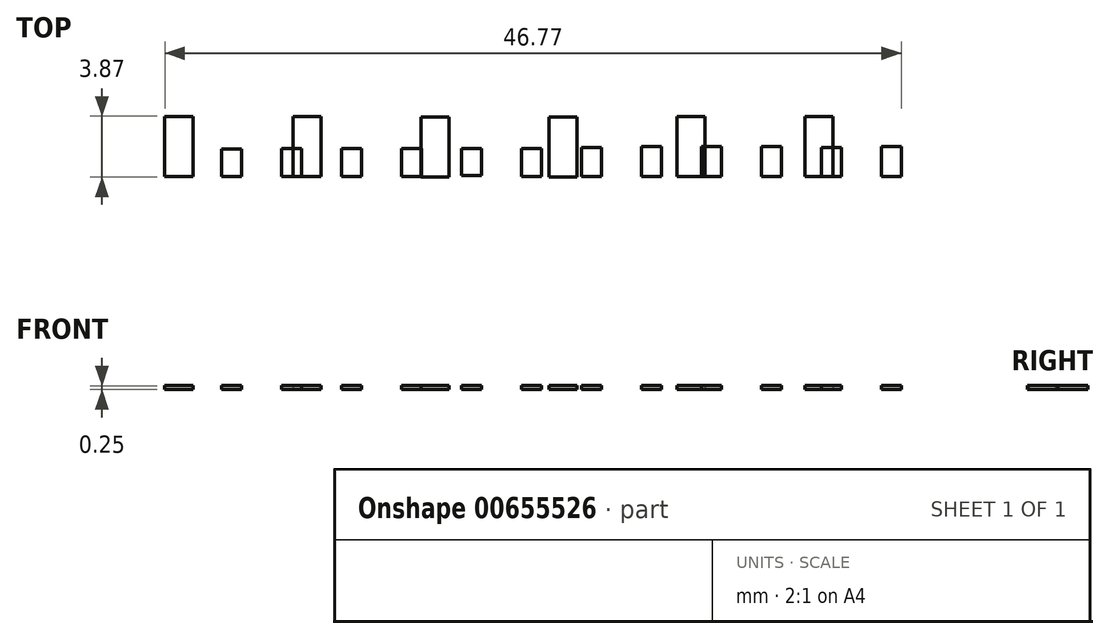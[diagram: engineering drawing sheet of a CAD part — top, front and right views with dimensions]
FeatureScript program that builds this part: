
annotation { "Feature Type Name" : "Feature", "Feature Type Description" : "" }
export const myFeature = defineFeature(function(context is Context, id is Id, definition is map)
    precondition{}
    {
        {
            var Q0;
            Q0=qCreatedBy(makeId("Top.planeOp"),FACE);
            var sketch = newSketch(context, id + "F0", { "sketchPlane" : qUnion([Q0])});
            skLineSegment(sketch, "E0.bottom", {"start": v(2.28, -12.7) * mm, "end": v(1.01, -12.7) * mm});
            skLineSegment(sketch, "E0.top", {"start": v(2.28, -10.86) * mm, "end": v(1.01, -10.86) * mm});
            skLineSegment(sketch, "E0.left", {"start": v(2.28, -12.7) * mm, "end": v(2.28, -10.86) * mm});
            skLineSegment(sketch, "E0.right", {"start": v(1.01, -12.7) * mm, "end": v(1.01, -10.86) * mm});
            skLineSegment(sketch, "E1.bottom", {"start": v(-1.53, -12.69) * mm, "end": v(-2.8, -12.69) * mm});
            skLineSegment(sketch, "E1.top", {"start": v(-1.53, -10.91) * mm, "end": v(-2.8, -10.91) * mm});
            skLineSegment(sketch, "E1.left", {"start": v(-1.53, -12.69) * mm, "end": v(-1.53, -10.91) * mm});
            skLineSegment(sketch, "E1.right", {"start": v(-2.8, -12.69) * mm, "end": v(-2.8, -10.91) * mm});
            skLineSegment(sketch, "E2.bottom", {"start": v(-5.34, -12.64) * mm, "end": v(-6.6, -12.64) * mm});
            skLineSegment(sketch, "E2.top", {"start": v(-5.34, -10.92) * mm, "end": v(-6.6, -10.92) * mm});
            skLineSegment(sketch, "E2.left", {"start": v(-5.34, -12.64) * mm, "end": v(-5.34, -10.92) * mm});
            skLineSegment(sketch, "E2.right", {"start": v(-6.6, -12.64) * mm, "end": v(-6.6, -10.92) * mm});
            skLineSegment(sketch, "E3.bottom", {"start": v(-9.15, -12.71) * mm, "end": v(-10.42, -12.71) * mm});
            skLineSegment(sketch, "E3.top", {"start": v(-9.15, -10.93) * mm, "end": v(-10.42, -10.93) * mm});
            skLineSegment(sketch, "E3.left", {"start": v(-9.15, -12.71) * mm, "end": v(-9.15, -10.93) * mm});
            skLineSegment(sketch, "E3.right", {"start": v(-10.42, -12.71) * mm, "end": v(-10.42, -10.93) * mm});
            skLineSegment(sketch, "E4.bottom", {"start": v(-12.96, -12.71) * mm, "end": v(-14.23, -12.71) * mm});
            skLineSegment(sketch, "E4.top", {"start": v(-12.96, -10.93) * mm, "end": v(-14.23, -10.93) * mm});
            skLineSegment(sketch, "E4.left", {"start": v(-12.96, -12.71) * mm, "end": v(-12.96, -10.93) * mm});
            skLineSegment(sketch, "E4.right", {"start": v(-14.23, -12.71) * mm, "end": v(-14.23, -10.93) * mm});
            skPoint(sketch, "E5.oppositeSnap0", {"position": v(-13.6, -10.93) * mm});
            skLineSegment(sketch, "E5.bottom", {"start": v(-16.77, -12.71) * mm, "end": v(-18.04, -12.71) * mm});
            skLineSegment(sketch, "E5.top", {"start": v(-16.77, -10.93) * mm, "end": v(-18.04, -10.93) * mm});
            skLineSegment(sketch, "E5.left", {"start": v(-16.77, -12.71) * mm, "end": v(-16.77, -10.93) * mm});
            skLineSegment(sketch, "E5.right", {"start": v(-18.04, -12.71) * mm, "end": v(-18.04, -10.93) * mm});
            skLineSegment(sketch, "E6.bottom", {"start": v(-20.58, -12.7) * mm, "end": v(-21.85, -12.7) * mm});
            skLineSegment(sketch, "E6.top", {"start": v(-20.58, -10.95) * mm, "end": v(-21.85, -10.95) * mm});
            skLineSegment(sketch, "E6.left", {"start": v(-20.58, -12.7) * mm, "end": v(-20.58, -10.95) * mm});
            skLineSegment(sketch, "E6.right", {"start": v(-21.85, -12.7) * mm, "end": v(-21.85, -10.95) * mm});
            skLineSegment(sketch, "E7.bottom", {"start": v(6.1, -12.7) * mm, "end": v(4.82, -12.7) * mm});
            skLineSegment(sketch, "E7.top", {"start": v(6.1, -10.8) * mm, "end": v(4.82, -10.8) * mm});
            skLineSegment(sketch, "E7.left", {"start": v(6.1, -12.7) * mm, "end": v(6.1, -10.8) * mm});
            skLineSegment(sketch, "E7.right", {"start": v(4.82, -12.7) * mm, "end": v(4.82, -10.8) * mm});
            skLineSegment(sketch, "E8.bottom", {"start": v(9.9, -12.7) * mm, "end": v(8.63, -12.7) * mm});
            skLineSegment(sketch, "E8.top", {"start": v(9.9, -10.8) * mm, "end": v(8.63, -10.8) * mm});
            skLineSegment(sketch, "E8.left", {"start": v(9.9, -12.7) * mm, "end": v(9.9, -10.8) * mm});
            skLineSegment(sketch, "E8.right", {"start": v(8.63, -12.7) * mm, "end": v(8.63, -10.8) * mm});
            skLineSegment(sketch, "E9.bottom", {"start": v(13.71, -12.7) * mm, "end": v(12.44, -12.7) * mm});
            skLineSegment(sketch, "E9.top", {"start": v(13.71, -10.8) * mm, "end": v(12.44, -10.8) * mm});
            skLineSegment(sketch, "E9.left", {"start": v(13.71, -12.7) * mm, "end": v(13.71, -10.8) * mm});
            skLineSegment(sketch, "E9.right", {"start": v(12.44, -12.7) * mm, "end": v(12.44, -10.8) * mm});
            skLineSegment(sketch, "E10.bottom", {"start": v(17.52, -12.7) * mm, "end": v(16.25, -12.7) * mm});
            skLineSegment(sketch, "E10.top", {"start": v(17.52, -10.85) * mm, "end": v(16.25, -10.85) * mm});
            skLineSegment(sketch, "E10.left", {"start": v(17.52, -12.7) * mm, "end": v(17.52, -10.85) * mm});
            skLineSegment(sketch, "E10.right", {"start": v(16.25, -12.7) * mm, "end": v(16.25, -10.85) * mm});
            skLineSegment(sketch, "E11.bottom", {"start": v(21.33, -12.7) * mm, "end": v(20.06, -12.7) * mm});
            skLineSegment(sketch, "E11.top", {"start": v(21.33, -10.8) * mm, "end": v(20.06, -10.8) * mm});
            skLineSegment(sketch, "E11.left", {"start": v(21.33, -12.7) * mm, "end": v(21.33, -10.8) * mm});
            skLineSegment(sketch, "E11.right", {"start": v(20.06, -12.7) * mm, "end": v(20.06, -10.8) * mm});
            skSolve(sketch);
        }
        {
            var Q0;
            Q0=qCreatedBy(makeId("Top.planeOp"),FACE);
            var sketch = newSketch(context, id + "F1", { "sketchPlane" : qUnion([Q0])});
            skLineSegment(sketch, "E12.bottom", {"start": v(-25.44, -12.7) * mm, "end": v(-23.66, -12.7) * mm});
            skLineSegment(sketch, "E12.top", {"start": v(-25.44, -8.9) * mm, "end": v(-23.66, -8.9) * mm});
            skLineSegment(sketch, "E12.left", {"start": v(-25.44, -12.7) * mm, "end": v(-25.44, -8.9) * mm});
            skLineSegment(sketch, "E12.right", {"start": v(-23.66, -12.7) * mm, "end": v(-23.66, -8.9) * mm});
            skLineSegment(sketch, "E13.bottom", {"start": v(-17.31, -12.7) * mm, "end": v(-15.53, -12.7) * mm});
            skLineSegment(sketch, "E13.top", {"start": v(-17.31, -8.9) * mm, "end": v(-15.53, -8.9) * mm});
            skLineSegment(sketch, "E13.left", {"start": v(-17.31, -12.7) * mm, "end": v(-17.31, -8.9) * mm});
            skLineSegment(sketch, "E13.right", {"start": v(-15.53, -12.7) * mm, "end": v(-15.53, -8.9) * mm});
            skLineSegment(sketch, "E14.bottom", {"start": v(-7.4, -12.74) * mm, "end": v(-9.18, -12.74) * mm});
            skLineSegment(sketch, "E14.top", {"start": v(-7.4, -8.93) * mm, "end": v(-9.18, -8.93) * mm});
            skLineSegment(sketch, "E14.left", {"start": v(-7.4, -12.74) * mm, "end": v(-7.4, -8.93) * mm});
            skLineSegment(sketch, "E14.right", {"start": v(-9.18, -12.74) * mm, "end": v(-9.18, -8.93) * mm});
            skLineSegment(sketch, "E15.bottom", {"start": v(-1.06, -12.74) * mm, "end": v(0.72, -12.74) * mm});
            skLineSegment(sketch, "E15.top", {"start": v(-1.06, -8.93) * mm, "end": v(0.72, -8.93) * mm});
            skLineSegment(sketch, "E15.left", {"start": v(0.72, -12.74) * mm, "end": v(0.72, -8.93) * mm});
            skLineSegment(sketch, "E15.right", {"start": v(-1.06, -12.74) * mm, "end": v(-1.06, -8.93) * mm});
            skLineSegment(sketch, "E16.bottom", {"start": v(15.2, -12.69) * mm, "end": v(16.98, -12.69) * mm});
            skLineSegment(sketch, "E16.top", {"start": v(15.2, -8.88) * mm, "end": v(16.98, -8.88) * mm});
            skLineSegment(sketch, "E16.left", {"start": v(16.98, -12.69) * mm, "end": v(16.98, -8.88) * mm});
            skLineSegment(sketch, "E16.right", {"start": v(15.2, -12.69) * mm, "end": v(15.2, -8.88) * mm});
            skLineSegment(sketch, "E17.bottom", {"start": v(7.07, -12.68) * mm, "end": v(8.85, -12.68) * mm});
            skLineSegment(sketch, "E17.top", {"start": v(7.07, -8.87) * mm, "end": v(8.85, -8.87) * mm});
            skLineSegment(sketch, "E17.left", {"start": v(8.85, -12.68) * mm, "end": v(8.85, -8.87) * mm});
            skLineSegment(sketch, "E17.right", {"start": v(7.07, -12.68) * mm, "end": v(7.07, -8.87) * mm});
            skLineSegment(sketch, "E18.left", {"start": v(22.53, -8.74) * mm, "end": v(22.53, -8.62) * mm});
            skPoint(sketch, "E19.oppositeSnap0", {"position": v(-25.44, -10.8) * mm});
            skSolve(sketch);
        }
        {
            var Q0;
            Q0=qSketchRegion(id+"F0",true);
            extrude(context, id + "F2", {"entities" : qUnion([Q0]), "depth" : 0.25 * mm, "offsetDistance" : 25.4 * mm});
        }
        {
            var Q0;
            Q0=qSketchRegion(id+"F1",true);
            extrude(context, id + "F3", {"entities" : qUnion([Q0]), "depth" : 0.25 * mm, "offsetDistance" : 25.4 * mm});
        }
    });
